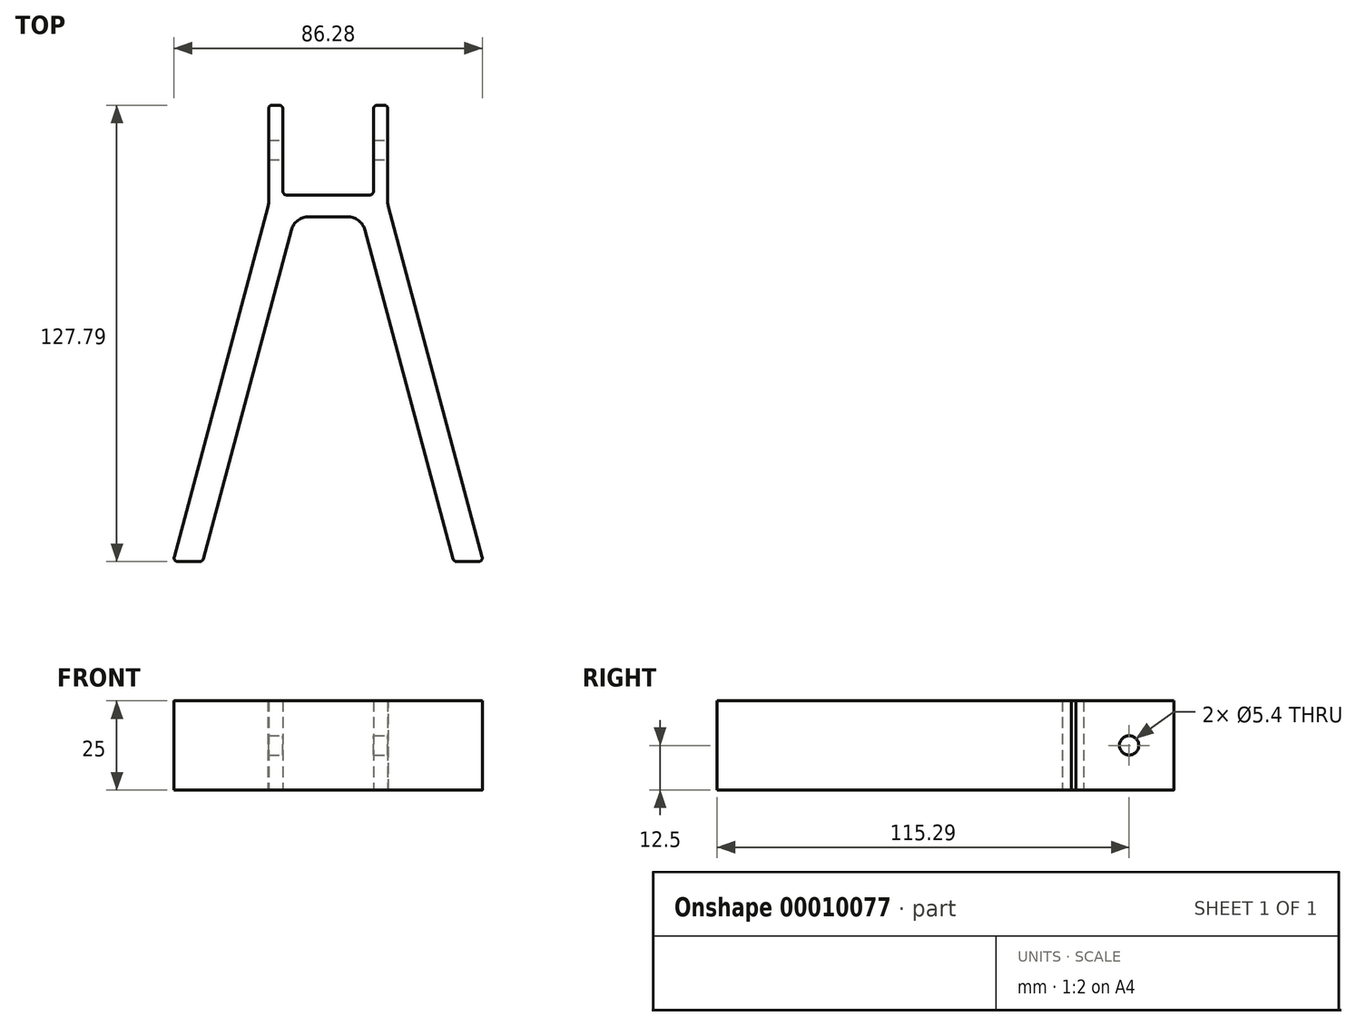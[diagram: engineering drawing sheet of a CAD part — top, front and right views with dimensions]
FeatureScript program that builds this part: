
annotation { "Feature Type Name" : "Feature", "Feature Type Description" : "" }
export const myFeature = defineFeature(function(context is Context, id is Id, definition is map)
    precondition{}
    {
        {
            var Q0;
            Q0=qCreatedBy(makeId("Top.planeOp"),FACE);
            var sketch = newSketch(context, id + "F5", { "sketchPlane" : qUnion([Q0])});
            skLineSegment(sketch, "E0.rect.bottom", {"start": v(16.7, 25.2) * mm, "end": v(12.7, 25.2) * mm});
            skLineSegment(sketch, "E0.rect.top", {"start": v(9.28, -6) * mm, "end": v(-9.28, -6) * mm});
            skPoint(sketch, "E0.rect.middle", {"position": v(0, 0) * mm});
            skLineSegment(sketch, "E1.top", {"start": v(-12.7, 0) * mm, "end": v(12.7, 0) * mm});
            skLineSegment(sketch, "E1.left", {"start": v(-12.7, 25.2) * mm, "end": v(-12.7, 0) * mm});
            skLineSegment(sketch, "E1.right", {"start": v(12.7, 25.2) * mm, "end": v(12.7, 0) * mm});
            skLineSegment(sketch, "E2.trimOffspring", {"start": v(-12.7, 25.2) * mm, "end": v(-16.7, 25.2) * mm});
            skLineSegment(sketch, "E3", {"start": v(-16.7, -2.8) * mm, "end": v(-43.44, -102.6) * mm});
            skLineSegment(sketch, "E4", {"start": v(-9.28, -6) * mm, "end": v(-35.16, -102.6) * mm});
            skLineSegment(sketch, "E5", {"start": v(-35.16, -102.6) * mm, "end": v(-43.44, -102.6) * mm});
            skLineSegment(sketch, "E6", {"start": v(16.7, -2.8) * mm, "end": v(43.44, -102.6) * mm});
            skLineSegment(sketch, "E7", {"start": v(35.16, -102.6) * mm, "end": v(9.28, -6) * mm});
            skLineSegment(sketch, "E8", {"start": v(43.44, -102.6) * mm, "end": v(35.16, -102.6) * mm});
            skPoint(sketch, "E9.orphan", {"position": v(-21.34, -20.52) * mm});
            skPoint(sketch, "E10.orphan", {"position": v(21.34, -20.52) * mm});
            skLineSegment(sketch, "E11", {"start": v(-16.7, 25.2) * mm, "end": v(-16.7, -2.8) * mm});
            skLineSegment(sketch, "E12", {"start": v(16.7, -2.8) * mm, "end": v(16.7, 25.2) * mm});
            skSolve(sketch);
        }
        {
            var Q0;
            Q0=makeQuery(id+"F5.imprint","IMPRINT",FACE,{"disambiguationData":[TD([[makeQuery(id+"F5.imprint","IMPRINT",EDGE,{"derivedFrom":sQuery(id+"F5.wireOp",EDGE,"E0.rect.bottom")}),1.0]])]});
            extrude(context, id + "F0", {"entities" : qUnion([Q0]), "depth" : 25 * mm});
        }
        {
            var Q0;
            Q0=makeQuery(id+"F0.opExtrude","SWEPT_EDGE",EDGE,{"disambiguationData":[OSD([sQuery(id+"F5.wireOp",EDGE,"E0.rect.top"),sQuery(id+"F5.wireOp",EDGE,"E4")])]});
            var Q1;
            Q1=makeQuery(id+"F0.opExtrude","SWEPT_EDGE",EDGE,{"disambiguationData":[OSD([sQuery(id+"F5.wireOp",EDGE,"E0.rect.top"),sQuery(id+"F5.wireOp",EDGE,"E7")])]});
            fillet(context, id + "F6", {"entities" : qUnion([Q0, Q1]), "radius" : 5 * mm, "tangentPropagation" : true, "allowEdgeOverflow" : false});
        }
        {
            var Q0;
            Q0=makeQuery(id+"F0.opExtrude","SWEPT_FACE",FACE,{"disambiguationData":[OSD([sQuery(id+"F5.wireOp",EDGE,"E12")])]});
            var sketch = newSketch(context, id + "F1", { "sketchPlane" : qUnion([Q0])});
            skCircle(sketch, "E13", {"center": v(12.7, 12.5) * mm, "radius": 2.7 * mm});
            skSolve(sketch);
        }
        {
            var Q0;
            Q0=qSketchRegion(id+"F1",true);
            extrude(context, id + "F2", {"entities" : qUnion([Q0]), "operationType" : NewBodyOperationType.REMOVE, "endBound" : BoundingType.THROUGH_ALL, "oppositeDirection" : true, "depth" : 25 * mm});
        }
        {
            var Q0;
            Q0=makeQuery(id+"F0.opExtrude","SWEPT_EDGE",EDGE,{"disambiguationData":[OSD([sQuery(id+"F5.wireOp",EDGE,"E3"),sQuery(id+"F5.wireOp",EDGE,"E11")])]});
            var Q1;
            Q1=makeQuery(id+"F0.opExtrude","SWEPT_EDGE",EDGE,{"disambiguationData":[OSD([sQuery(id+"F5.wireOp",EDGE,"E6"),sQuery(id+"F5.wireOp",EDGE,"E12")])]});
            chamfer(context, id + "F7", {"entities" : qUnion([Q0, Q1]), "width" : 5 * mm, "tangentPropagation" : true});
        }
        {
            var Q0;
            Q0=makeQuery(id+"F0.opExtrude","SWEPT_EDGE",EDGE,{"disambiguationData":[OSD([sQuery(id+"F5.wireOp",EDGE,"E1.left"),sQuery(id+"F5.wireOp",EDGE,"E2.trimOffspring")])]});
            var Q1;
            Q1=makeQuery(id+"F0.opExtrude","SWEPT_EDGE",EDGE,{"disambiguationData":[OSD([sQuery(id+"F5.wireOp",EDGE,"E2.trimOffspring"),sQuery(id+"F5.wireOp",EDGE,"E11")])]});
            var Q2;
            Q2=makeQuery(id+"F0.opExtrude","SWEPT_EDGE",EDGE,{"disambiguationData":[OSD([sQuery(id+"F5.wireOp",EDGE,"E0.rect.bottom"),sQuery(id+"F5.wireOp",EDGE,"E12")])]});
            var Q3;
            Q3=makeQuery(id+"F0.opExtrude","SWEPT_EDGE",EDGE,{"disambiguationData":[OSD([sQuery(id+"F5.wireOp",EDGE,"E4"),sQuery(id+"F5.wireOp",EDGE,"E5")])]});
            var Q4;
            Q4=makeQuery(id+"F0.opExtrude","SWEPT_EDGE",EDGE,{"disambiguationData":[OSD([sQuery(id+"F5.wireOp",EDGE,"E3"),sQuery(id+"F5.wireOp",EDGE,"E5")])]});
            var Q5;
            Q5=makeQuery(id+"F0.opExtrude","SWEPT_EDGE",EDGE,{"disambiguationData":[OSD([sQuery(id+"F5.wireOp",EDGE,"E7"),sQuery(id+"F5.wireOp",EDGE,"E8")])]});
            var Q6;
            Q6=makeQuery(id+"F0.opExtrude","SWEPT_EDGE",EDGE,{"disambiguationData":[OSD([sQuery(id+"F5.wireOp",EDGE,"E6"),sQuery(id+"F5.wireOp",EDGE,"E8")])]});
            var Q7;
            Q7=makeQuery(id+"F0.opExtrude","SWEPT_EDGE",EDGE,{"disambiguationData":[OSD([sQuery(id+"F5.wireOp",EDGE,"E0.rect.bottom"),sQuery(id+"F5.wireOp",EDGE,"E1.right")])]});
            fillet(context, id + "F3", {"entities" : qUnion([Q0, Q1, Q2, Q3, Q4, Q5, Q6, Q7]), "radius" : 1 * mm, "tangentPropagation" : true, "allowEdgeOverflow" : false});
        }
        {
            var Q0;
            Q0=makeQuery(id+"F0.opExtrude","SWEPT_EDGE",EDGE,{"disambiguationData":[OSD([sQuery(id+"F5.wireOp",EDGE,"E1.top"),sQuery(id+"F5.wireOp",EDGE,"E1.left")])]});
            var Q1;
            Q1=makeQuery(id+"F0.opExtrude","SWEPT_EDGE",EDGE,{"disambiguationData":[OSD([sQuery(id+"F5.wireOp",EDGE,"E1.top"),sQuery(id+"F5.wireOp",EDGE,"E1.right")])]});
            fillet(context, id + "F4", {"entities" : qUnion([Q0, Q1]), "radius" : 1.2 * mm, "tangentPropagation" : true, "allowEdgeOverflow" : false});
        }
    });
